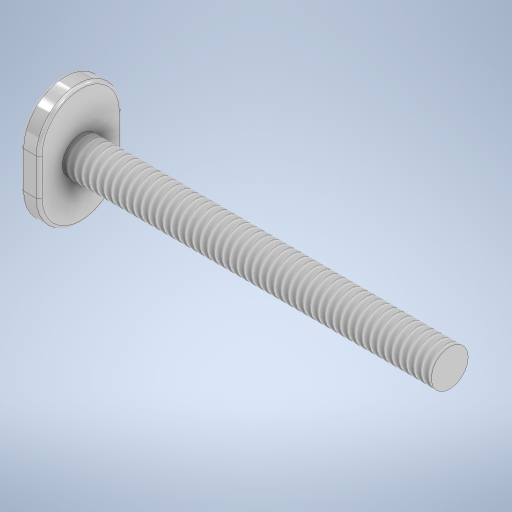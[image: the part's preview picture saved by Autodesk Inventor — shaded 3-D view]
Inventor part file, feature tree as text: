
AUTODESK INVENTOR PART (.ipt)
format: ipt  version: 2024 (Build 280153000, 153)  size: 305,152 bytes
history: native  units: in
note: dims shown in document units (in); Inventor stores cm internally (conversion verified against a paired STEP export)
features: extrude x2, sketch x2, thread x1, fillet x1
ambient origin geometry x8: Origin, YZ Plane, XZ Plane, XY Plane, X Axis, Y Axis, Z Axis, Center Point
bodies: Solid1 (feature_tree)
feature tree (6):
  extrude  "Extrusion1"  Depth=0.563in
  extrude  "Extrusion2"  Depth=0.125in TaperAngle=0.0deg
  thread  "Thread1"  [1 undecoded]
  fillet  "Fillet1"  Radius=2.5in
  sketch  "Sketch1"  dims[d0=0.8125in d1=0.563in]
  sketch  "Sketch2"  dims[d2=0.2815in d3=0.125in d4=0.0in d5=2.5in d6=0.0in d7=2.5in d8=0.0in d9=0.02in]
note: 1 required parameter value undecoded (feature->parameter linkage not recoverable at this tier; creation-order binding heuristic only, values carry confidence <= 0.55)
